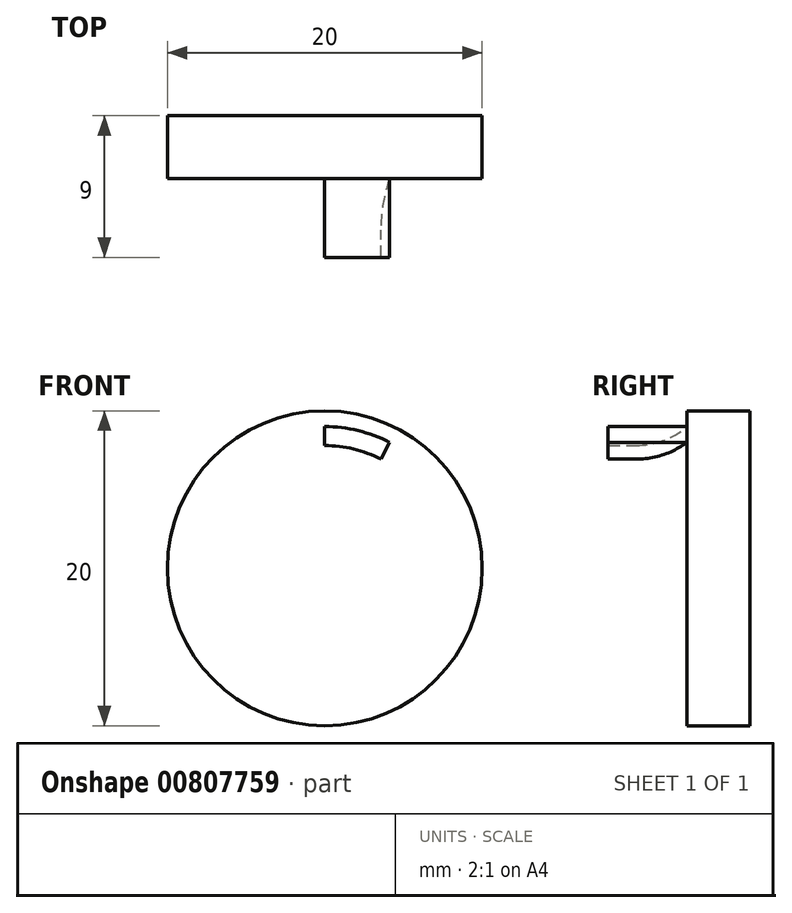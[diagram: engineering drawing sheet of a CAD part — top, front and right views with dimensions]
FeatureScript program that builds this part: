
annotation { "Feature Type Name" : "Feature", "Feature Type Description" : "" }
export const myFeature = defineFeature(function(context is Context, id is Id, definition is map)
    precondition{}
    {
        {
            var Q0;
            Q0=qCreatedBy(makeId("Front.planeOp"),FACE);
            var sketch = newSketch(context, id + "F0", { "sketchPlane" : qUnion([Q0])});
            skCircle(sketch, "E0", {"center": v(0, 0) * mm, "radius": 10 * mm});
            skCircle(sketch, "E1", {"center": v(0, 3.5) * mm, "radius": 13.5 * mm});
            skLineSegment(sketch, "E2", {"start": v(0, 3.5) * mm, "end": v(0, 0) * mm, "construction": true});
            skSolve(sketch);
        }
        {
            var Q0;
            Q0=qCreatedBy(makeId("Front.planeOp"),FACE);
            var sketch = newSketch(context, id + "F1", { "sketchPlane" : qUnion([Q0])});
            skCircle(sketch, "E3.0", {"center": v(0, 0) * mm, "radius": 10 * mm});
            skCircle(sketch, "E4", {"center": v(0, 0) * mm, "radius": 9 * mm});
            skCircle(sketch, "E5", {"center": v(0, 0) * mm, "radius": 7.8 * mm});
            skLineSegment(sketch, "E6", {"start": v(0, 7.8) * mm, "end": v(0, 9) * mm});
            skLineSegment(sketch, "E7", {"start": v(3.57, 6.93) * mm, "end": v(4.12, 8) * mm});
            skSolve(sketch);
        }
        {
            var Q0;
            {var subQ0=sQuery(id+"F1.wireOp",EDGE,"E6");Q0=makeQuery(id+"F1.imprint","IMPRINT",FACE,{"disambiguationData":[TD([[makeQuery(id+"F1.imprint","IMPRINT",EDGE,{"derivedFrom":subQ0}),-1.0]])]});}
            extrude(context, id + "F2", {"entities" : qUnion([Q0]), "depth" : 5 * mm, "offsetDistance" : 25 * mm});
        }
        {
            var Q0;
            Q0=qCreatedBy(makeId("Top.planeOp"),FACE);
            var sketch = newSketch(context, id + "F3", { "sketchPlane" : qUnion([Q0])});
            skPoint(sketch, "E8.0", {"position": v(0, 0) * mm});
            skLineSegment(sketch, "E9", {"start": v(0, 0) * mm, "end": v(0, -40.14) * mm});
            skSolve(sketch);
        }
        {
            var Q0;
            Q0=qCreatedBy(makeId("Front.planeOp"),FACE);
            var sketch = newSketch(context, id + "F4", { "sketchPlane" : qUnion([Q0])});
            skCircle(sketch, "E10.0", {"center": v(0, 3.5) * mm, "radius": 13.5 * mm});
            skSolve(sketch);
        }
        {
            var Q0;
            Q0=makeQuery(id+"F4.imprint","IMPRINT",FACE,{"disambiguationData":[TD([[makeQuery(id+"F4.imprint","IMPRINT",EDGE,{"derivedFrom":sQuery(id+"F4.wireOp",EDGE,"E10.0")}),1.0]])]});
            extrude(context, id + "F5", {"entities" : qUnion([Q0]), "oppositeDirection" : true, "depth" : 4 * mm, "offsetDistance" : 25 * mm});
        }
        {
            var Q0;
            Q0=makeQuery(id+"FcTL8sork1jxCOk_1.1.F2.opExtrude","CAP_EDGE",EDGE,{"disambiguationData":[OSD([sQuery(id+"F1.wireOp",EDGE,"E5")])],"isStart":true});
            var Q1;
            Q1=makeQuery(id+"F2.opExtrude","CAP_EDGE",EDGE,{"disambiguationData":[OSD([sQuery(id+"F1.wireOp",EDGE,"E5")])],"isStart":true});
            var Q2;
            Q2=makeQuery(id+"FcTL8sork1jxCOk_1.5.F2.opExtrude","CAP_EDGE",EDGE,{"disambiguationData":[OSD([sQuery(id+"F1.wireOp",EDGE,"E5")])],"isStart":true});
            var Q3;
            Q3=makeQuery(id+"FcTL8sork1jxCOk_1.4.F2.opExtrude","CAP_EDGE",EDGE,{"disambiguationData":[OSD([sQuery(id+"F1.wireOp",EDGE,"E5")])],"isStart":true});
            var Q4;
            Q4=makeQuery(id+"FcTL8sork1jxCOk_1.3.F2.opExtrude","CAP_EDGE",EDGE,{"disambiguationData":[OSD([sQuery(id+"F1.wireOp",EDGE,"E5")])],"isStart":true});
            var Q5;
            Q5=makeQuery(id+"FcTL8sork1jxCOk_1.2.F2.opExtrude","CAP_EDGE",EDGE,{"disambiguationData":[OSD([sQuery(id+"F1.wireOp",EDGE,"E5")])],"isStart":true});
            fillet(context, id + "F6", {"entities" : qUnion([Q0, Q1, Q2, Q3, Q4, Q5]), "radius" : 5 * mm, "tangentPropagation" : true, "allowEdgeOverflow" : false});
        }
        {
            var Q0;
            Q0=makeQuery(id+"F0.imprint","IMPRINT",FACE,{"disambiguationData":[TD([[makeQuery(id+"F0.imprint","IMPRINT",EDGE,{"derivedFrom":sQuery(id+"F0.wireOp",EDGE,"E0")}),-1.0]])]});
            var sketch = newSketch(context, id + "F7", { "sketchPlane" : qUnion([Q0])});
            skCircle(sketch, "E11.0", {"center": v(0, 0) * mm, "radius": 10 * mm});
            skArc(sketch, "E12", {"start": v(11.41, -3.71) * mm, "mid": v(0, 12) * mm, "end": v(-11.41, -3.71) * mm});
            skCircle(sketch, "E13.0", {"center": v(0, 3.5) * mm, "radius": 13.5 * mm});
            skLineSegment(sketch, "E14", {"start": v(0, 0) * mm, "end": v(-12, 0) * mm});
            skLineSegment(sketch, "E15", {"start": v(0, 0) * mm, "end": v(12, 0) * mm});
            skSolve(sketch);
        }
        {
            var Q0;
            {var subQ0=sQuery(id+"F7.wireOp",EDGE,"E14");var subQ1=sQuery(id+"F7.wireOp",EDGE,"E11.0");var subQ2=makeQuery(id+"F7.imprint","INTERSECT",VERTEX,{"derivedFrom":[subQ1,subQ0]});Q0=makeQuery(id+"F7.imprint","IMPRINT",FACE,{"disambiguationData":[TD([[makeQuery(id+"F7.imprint","IMPRINT",EDGE,{"disambiguationData":[TD([[subQ2,1.0]])],"derivedFrom":subQ1}),-1.0]])]});}
            extrude(context, id + "F8", {"entities" : qUnion([Q0]), "operationType" : NewBodyOperationType.ADD, "depth" : 6 * mm, "offsetDistance" : 25 * mm});
        }
        {
            var Q0;
            Q0=makeQuery(id+"F8.opExtrude","CAP_FACE",FACE,{"disambiguationData":[OSD([sQuery(id+"F7.wireOp",EDGE,"E11.0"),sQuery(id+"F7.wireOp",EDGE,"E12"),sQuery(id+"F7.wireOp",EDGE,"E14"),sQuery(id+"F7.wireOp",EDGE,"E15")])],"isStart":false});
            var sketch = newSketch(context, id + "F9", { "sketchPlane" : qUnion([Q0])});
            skArc(sketch, "E16.0", {"start": v(13.5, 0) * mm, "mid": v(0, 13.5) * mm, "end": v(-13.5, 0) * mm});
            skLineSegment(sketch, "E17", {"start": v(-13.5, 0) * mm, "end": v(-12, 0) * mm});
            skLineSegment(sketch, "E18", {"start": v(12, 0) * mm, "end": v(13.5, 0) * mm});
            skArc(sketch, "E19.0", {"start": v(12, 0) * mm, "mid": v(0, 12) * mm, "end": v(-12, 0) * mm});
            skPoint(sketch, "E20.0", {"position": v(-10, 0) * mm});
            skLineSegment(sketch, "E21.0", {"start": v(-10, 0) * mm, "end": v(-12, 0) * mm});
            skArc(sketch, "E22.0", {"start": v(10, 0) * mm, "mid": v(0, 10) * mm, "end": v(-10, 0) * mm});
            skLineSegment(sketch, "E23.0", {"start": v(10, 0) * mm, "end": v(12, 0) * mm});
            skSolve(sketch);
        }
        {
            var Q0;
            Q0=makeQuery(id+"F9.imprint","IMPRINT",FACE,{"disambiguationData":[TD([[makeQuery(id+"F9.imprint","IMPRINT",EDGE,{"derivedFrom":sQuery(id+"F9.wireOp",EDGE,"E16.0")}),1.0]])]});
            var Q1;
            Q1=makeQuery(id+"F9.imprint","IMPRINT",FACE,{"disambiguationData":[TD([[makeQuery(id+"F9.imprint","IMPRINT",EDGE,{"derivedFrom":sQuery(id+"F9.wireOp",EDGE,"E19.0")}),1.0]])]});
            extrude(context, id + "F10", {"entities" : qUnion([Q0, Q1]), "operationType" : NewBodyOperationType.ADD, "depth" : 1.5 * mm, "offsetDistance" : 25 * mm});
        }
        {
            var Q0;
            Q0=makeQuery(id+"F5.opExtrude","CAP_FACE",FACE,{"disambiguationData":[OSD([sQuery(id+"F4.wireOp",EDGE,"E10.0")])],"isStart":false});
            var sketch = newSketch(context, id + "F11", { "sketchPlane" : qUnion([Q0])});
            skPoint(sketch, "E24.0", {"position": v(0, 0) * mm});
            skCircle(sketch, "E25", {"center": v(0, 0) * mm, "radius": 10 * mm});
            skCircle(sketch, "E26", {"center": v(0, 0) * mm, "radius": 23.18 * mm});
            skSolve(sketch);
        }
        {
            var Q0;
            Q0=makeQuery(id+"F11.imprint","IMPRINT",FACE,{"disambiguationData":[TD([[makeQuery(id+"F11.imprint","IMPRINT",EDGE,{"derivedFrom":sQuery(id+"F11.wireOp",EDGE,"E26")}),1.0]])]});
            var Q1;
            Q1=makeQuery(id+"F11.imprint","IMPRINT",FACE,{"disambiguationData":[TD([[makeQuery(id+"F11.imprint","IMPRINT",EDGE,{"derivedFrom":sQuery(id+"F11.wireOp",EDGE,"E25")}),-1.0]])]});
            extrude(context, id + "F12", {"entities" : qUnion([Q0, Q1]), "operationType" : NewBodyOperationType.REMOVE, "oppositeDirection" : true, "depth" : 25 * mm, "offsetDistance" : 25 * mm});
        }
    });
